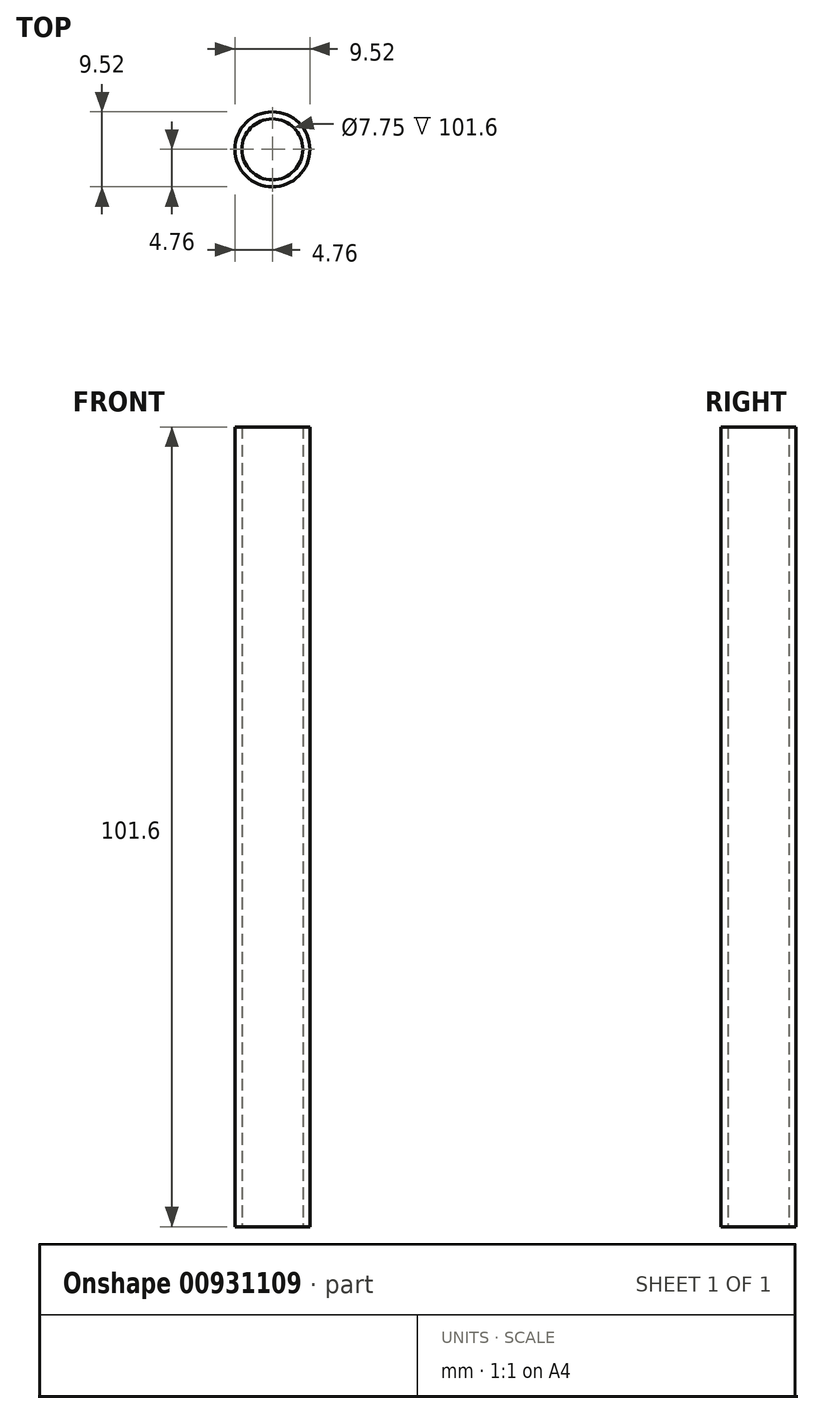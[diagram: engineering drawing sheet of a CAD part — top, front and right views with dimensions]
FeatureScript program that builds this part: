
annotation { "Feature Type Name" : "Feature", "Feature Type Description" : "" }
export const myFeature = defineFeature(function(context is Context, id is Id, definition is map)
    precondition{}
    {
        {
            var Q0;
            Q0=qCreatedBy(makeId("Top.planeOp"),FACE);
            var sketch = newSketch(context, id + "F0", { "sketchPlane" : qUnion([Q0])});
            skCircle(sketch, "E0", {"center": v(0, 0) * mm, "radius": 4.76 * mm});
            skCircle(sketch, "E1", {"center": v(0, 0) * mm, "radius": 3.87 * mm});
            skSolve(sketch);
        }
        {
            var Q0;
            Q0=makeQuery(id+"F0.imprint","IMPRINT",FACE,{"disambiguationData":[TD([[makeQuery(id+"F0.imprint","IMPRINT",EDGE,{"derivedFrom":sQuery(id+"F0.wireOp",EDGE,"E0")}),1.0]])]});
            extrude(context, id + "F1", {"entities" : qUnion([Q0]), "depth" : 101.6 * mm, "offsetDistance" : 25.4 * mm});
        }
    });
